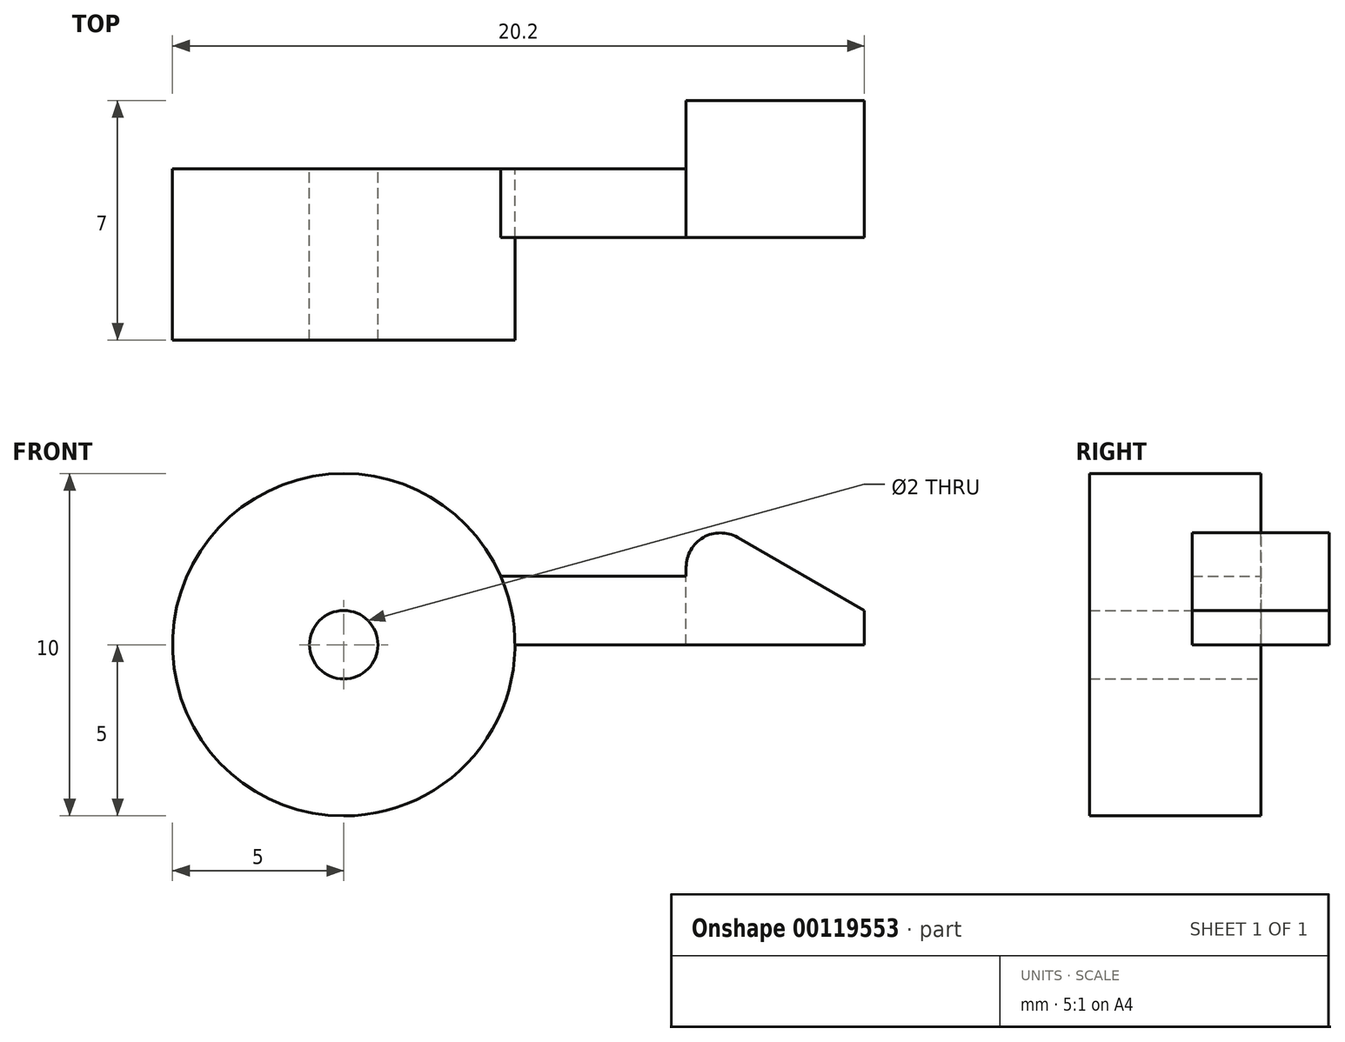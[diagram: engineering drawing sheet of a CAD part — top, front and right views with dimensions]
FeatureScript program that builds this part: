
annotation { "Feature Type Name" : "Feature", "Feature Type Description" : "" }
export const myFeature = defineFeature(function(context is Context, id is Id, definition is map)
    precondition{}
    {
        {
            var Q0;
            Q0=qCreatedBy(makeId("Front.planeOp"),FACE);
            var sketch = newSketch(context, id + "F0", { "sketchPlane" : qUnion([Q0])});
            skCircle(sketch, "E0", {"center": v(0, 0) * mm, "radius": 5 * mm});
            skLineSegment(sketch, "E1", {"start": v(5, 0) * mm, "end": v(10, 0) * mm});
            skLineSegment(sketch, "E2", {"start": v(10, 0) * mm, "end": v(10, 2) * mm});
            skLineSegment(sketch, "E3", {"start": v(10, 2) * mm, "end": v(4.58, 2) * mm});
            skLineSegment(sketch, "E4", {"start": v(10, 2) * mm, "end": v(10, 4) * mm});
            skLineSegment(sketch, "E5", {"start": v(10, 4) * mm, "end": v(15.2, 1) * mm});
            skLineSegment(sketch, "E6", {"start": v(15.2, 1) * mm, "end": v(15.2, 0) * mm});
            skLineSegment(sketch, "E7", {"start": v(15.2, 0) * mm, "end": v(10, 0) * mm});
            skSolve(sketch);
        }
        {
            var Q0;
            {var subQ0=sQuery(id+"F0.wireOp",EDGE,"E0");var subQ1=makeQuery(id+"F0.imprint","INTERSECT",VERTEX,{"derivedFrom":[subQ0,sQuery(id+"F0.wireOp",EDGE,"E1")]});Q0=makeQuery(id+"F0.imprint","IMPRINT",FACE,{"disambiguationData":[TD([[makeQuery(id+"F0.imprint","IMPRINT",EDGE,{"disambiguationData":[TD([[subQ1,-1.0]])],"derivedFrom":subQ0}),1.0]])]});}
            extrude(context, id + "F1", {"entities" : qUnion([Q0]), "depth" : 5 * mm});
        }
        {
            var Q0;
            {var subQ0=sQuery(id+"F0.wireOp",EDGE,"E1");Q0=makeQuery(id+"F0.imprint","IMPRINT",FACE,{"disambiguationData":[TD([[makeQuery(id+"F0.imprint","IMPRINT",EDGE,{"derivedFrom":subQ0}),1.0]])]});}
            extrude(context, id + "F2", {"entities" : qUnion([Q0]), "operationType" : NewBodyOperationType.ADD, "depth" : 2 * mm});
        }
        {
            var Q0;
            Q0=makeQuery(id+"F0.imprint","IMPRINT",FACE,{"disambiguationData":[TD([[makeQuery(id+"F0.imprint","IMPRINT",EDGE,{"derivedFrom":sQuery(id+"F0.wireOp",EDGE,"E2")}),-1.0]])]});
            extrude(context, id + "F3", {"entities" : qUnion([Q0]), "operationType" : NewBodyOperationType.ADD, "endBound" : BoundingType.SYMMETRIC, "depth" : 4 * mm});
        }
        {
            var Q0;
            Q0=sQuery(id+"F0.wireOp",VERTEX,"E0.center");
            var Q1;
            Q1=makeQuery(id+"F1.opExtrude","SWEPT_BODY",BODY,{"disambiguationData":[OSD([sQuery(id+"F0.wireOp",EDGE,"E0")])]});
            hole(context, id + "F4", {"style" : HoleStyle.SIMPLE, "endStyle" : HoleEndStyle.THROUGH, "oppositeDirection" : true, "holeDiameter" : 2 * mm, "locations" : qUnion([Q0]), "scope" : qUnion([Q1]), "isTappedThrough" : true});
        }
        {
            var Q0;
            Q0=makeQuery(id+"F3.opExtrude","SWEPT_EDGE",EDGE,{"disambiguationData":[OSD([sQuery(id+"F0.wireOp",EDGE,"E4"),sQuery(id+"F0.wireOp",EDGE,"E5")])]});
            fillet(context, id + "F5", {"entities" : qUnion([Q0]), "radius" : 1 * mm, "tangentPropagation" : true, "allowEdgeOverflow" : false});
        }
    });
